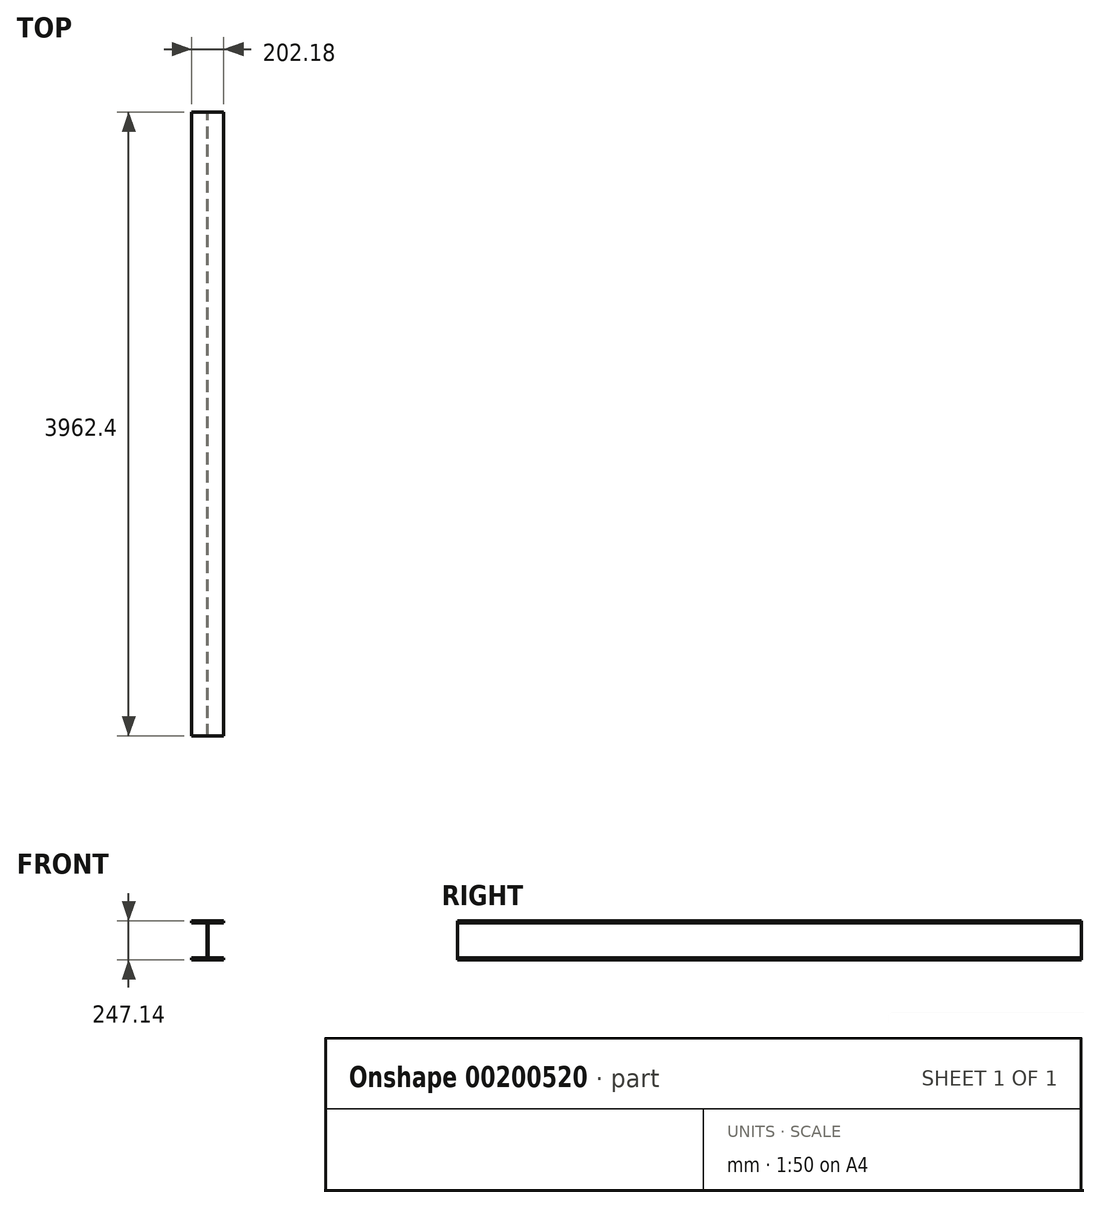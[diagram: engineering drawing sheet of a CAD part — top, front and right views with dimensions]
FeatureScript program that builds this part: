
annotation { "Feature Type Name" : "Feature", "Feature Type Description" : "" }
export const myFeature = defineFeature(function(context is Context, id is Id, definition is map)
    precondition{}
    {
        {
            var Q0;
            Q0=qCreatedBy(makeId("Front.planeOp"),FACE);
            var sketch = newSketch(context, id + "F0", { "sketchPlane" : qUnion([Q0])});
            skLineSegment(sketch, "E0", {"start": v(101.1, 0) * mm, "end": v(101.1, 11.05) * mm});
            skLineSegment(sketch, "E1", {"start": v(101.1, 11.05) * mm, "end": v(3.68, 11.05) * mm});
            skLineSegment(sketch, "E2", {"start": v(3.68, 11.05) * mm, "end": v(3.68, 236.1) * mm});
            skLineSegment(sketch, "E3", {"start": v(3.68, 236.1) * mm, "end": v(101.1, 236.1) * mm});
            skLineSegment(sketch, "E4", {"start": v(101.1, 236.1) * mm, "end": v(101.1, 247.14) * mm});
            skLineSegment(sketch, "E5", {"start": v(101.1, 247.14) * mm, "end": v(0, 247.14) * mm});
            skLineSegment(sketch, "E6", {"start": v(101.1, 0) * mm, "end": v(0, 0) * mm});
            skLineSegment(sketch, "E7", {"start": v(0, -24.07) * mm, "end": v(0, 108.97) * mm, "construction": true});
            skLineSegment(sketch, "E8.MirrorCS", {"start": v(-101.1, 236.1) * mm, "end": v(-101.1, 247.14) * mm});
            skLineSegment(sketch, "E9.MirrorCS", {"start": v(-101.1, 0) * mm, "end": v(-101.1, 11.05) * mm});
            skLineSegment(sketch, "E10.MirrorCS", {"start": v(-101.1, 11.05) * mm, "end": v(-3.68, 11.05) * mm});
            skLineSegment(sketch, "E11.MirrorCS", {"start": v(-3.68, 11.05) * mm, "end": v(-3.68, 236.1) * mm});
            skLineSegment(sketch, "E12.MirrorCS", {"start": v(-3.68, 236.1) * mm, "end": v(-101.1, 236.1) * mm});
            skLineSegment(sketch, "E13.MirrorCS", {"start": v(-101.1, 247.14) * mm, "end": v(0, 247.14) * mm});
            skLineSegment(sketch, "E14.MirrorCS", {"start": v(-101.1, 0) * mm, "end": v(0, 0) * mm});
            skSolve(sketch);
        }
        {
            var Q0;
            Q0 = qSketchRegion(id + "F0", true);
            extrude(context, id + "F1", {"entities" : qUnion([Q0]), "depth" : 3962.4 * mm, "offsetDistance" : 25.4 * mm});
        }
    });
